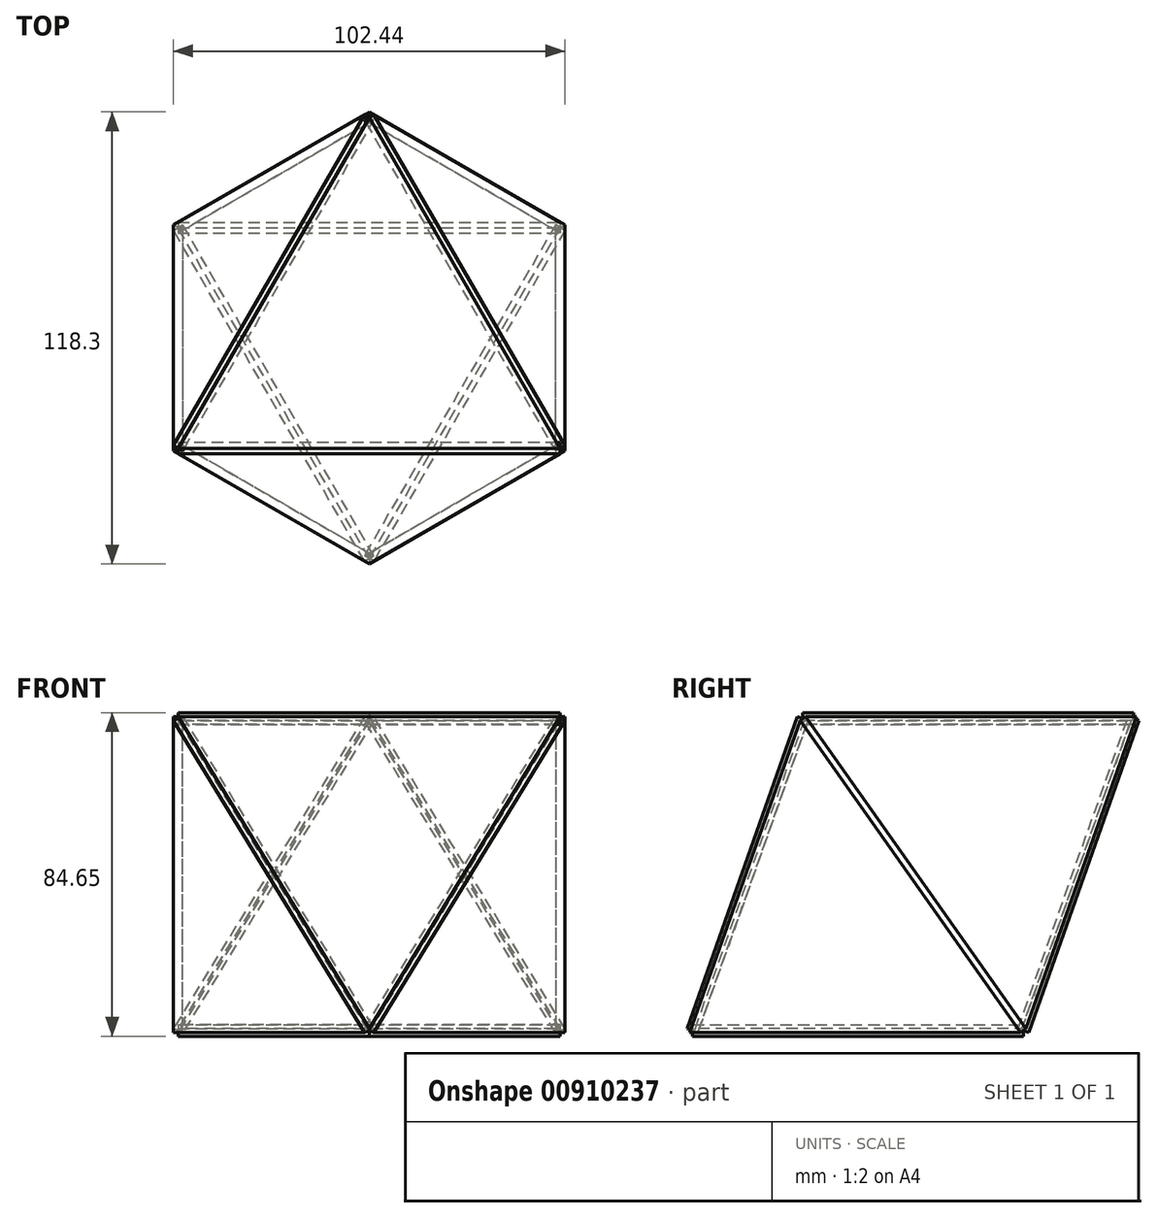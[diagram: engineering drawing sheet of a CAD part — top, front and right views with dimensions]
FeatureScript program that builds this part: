
annotation { "Feature Type Name" : "Feature", "Feature Type Description" : "" }
export const myFeature = defineFeature(function(context is Context, id is Id, definition is map)
    precondition{}
    {
        {
            var Q0;
            Q0=qCreatedBy(makeId("Top.planeOp"),FACE);
            var sketch = newSketch(context, id + "F0", { "sketchPlane" : qUnion([Q0])});
            skCircle(sketch, "E0.cCircle", {"center": v(0, 0) * mm, "radius": 28.87 * mm, "construction": true});
            skLineSegment(sketch, "E0.0", {"start": v(-50, 28.87) * mm, "end": v(50, 28.87) * mm});
            skLineSegment(sketch, "E0.1", {"start": v(50, 28.87) * mm, "end": v(0, -57.74) * mm});
            skLineSegment(sketch, "E0.2", {"start": v(0, -57.74) * mm, "end": v(-50, 28.87) * mm});
            skPoint(sketch, "E0.0.midPoint", {"position": v(0, 28.87) * mm});
            skSolve(sketch);
        }
        {
            var Q0;
            Q0=makeQuery(id+"F0.imprint","IMPRINT",FACE,{"disambiguationData":[TD([[makeQuery(id+"F0.imprint","IMPRINT",EDGE,{"derivedFrom":sQuery(id+"F0.wireOp",EDGE,"E0.0")}),-1.0]])]});
            extrude(context, id + "F1", {"entities" : qUnion([Q0]), "depth" : 3 * mm, "offsetDistance" : 25 * mm});
        }
        {
            var Q0;
            Q0=makeQuery(id+"F1.opExtrude","SWEPT_FACE",FACE,{"disambiguationData":[OSD([sQuery(id+"F0.wireOp",EDGE,"E0.2")])]});
            var sketch = newSketch(context, id + "F2", { "sketchPlane" : qUnion([Q0])});
            skLineSegment(sketch, "E1", {"start": v(-50, 1.5) * mm, "end": v(50, 1.5) * mm});
            skSolve(sketch);
        }
        {
            var Q0;
            Q0=makeQuery(id+"F1.opExtrude","SWEPT_BODY",BODY,{"disambiguationData":[OSD([sQuery(id+"F0.wireOp",EDGE,"E0.0"),sQuery(id+"F0.wireOp",EDGE,"E0.1"),sQuery(id+"F0.wireOp",EDGE,"E0.2")])]});
            transform(context, id + "F3", {"entities" : qUnion([Q0]), "transformType" : TransformType.TRANSLATION_3D, "dx" : 0 * mm, "dy" : 0 * mm, "dz" : 0 * mm, "makeCopy" : true});
        }
        {
            var Q0;
            Q0=makeQuery(id+"F3.opPattern","COPY",BODY,{"derivedFrom":makeQuery(id+"F1.opExtrude","SWEPT_BODY",BODY,{"disambiguationData":[OSD([sQuery(id+"F0.wireOp",EDGE,"E0.0"),sQuery(id+"F0.wireOp",EDGE,"E0.1"),sQuery(id+"F0.wireOp",EDGE,"E0.2")])]}),"instanceName":"1"});
            var Q1;
            Q1=sQuery(id+"F2.wireOp",EDGE,"E1");
            var Q2;
            Q2=sQuery(id+"F2.wireOp",EDGE,"E1");
            transform(context, id + "F4", {"entities" : qUnion([Q0]), "transformType" : TransformType.ROTATION, "transformAxis" : qUnion([Q2]), "angle" : 109.47 * degree, "makeCopy" : false});
        }
        {
            var Q0;
            Q0=makeQuery(id+"F1.opExtrude","SWEPT_BODY",BODY,{"disambiguationData":[OSD([sQuery(id+"F0.wireOp",EDGE,"E0.0"),sQuery(id+"F0.wireOp",EDGE,"E0.1"),sQuery(id+"F0.wireOp",EDGE,"E0.2")])]});
            transform(context, id + "F5", {"entities" : qUnion([Q0]), "transformType" : TransformType.TRANSLATION_3D, "dx" : 0 * mm, "dy" : 0 * mm, "dz" : 0 * mm, "makeCopy" : true});
        }
        {
            var Q0;
            Q0=makeQuery(id+"F1.opExtrude","SWEPT_FACE",FACE,{"disambiguationData":[OSD([sQuery(id+"F0.wireOp",EDGE,"E0.0")])]});
            var sketch = newSketch(context, id + "F6", { "sketchPlane" : qUnion([Q0])});
            skLineSegment(sketch, "E2", {"start": v(50, 1.5) * mm, "end": v(-50, 1.5) * mm});
            skSolve(sketch);
        }
        {
            var Q0;
            Q0=makeQuery(id+"F5.opPattern","COPY",BODY,{"derivedFrom":makeQuery(id+"F1.opExtrude","SWEPT_BODY",BODY,{"disambiguationData":[OSD([sQuery(id+"F0.wireOp",EDGE,"E0.0"),sQuery(id+"F0.wireOp",EDGE,"E0.1"),sQuery(id+"F0.wireOp",EDGE,"E0.2")])]}),"instanceName":"1"});
            var Q1;
            Q1=sQuery(id+"F6.wireOp",EDGE,"E2");
            var Q2;
            Q2=sQuery(id+"F6.wireOp",EDGE,"E2");
            transform(context, id + "F7", {"entities" : qUnion([Q0]), "transformType" : TransformType.ROTATION, "transformAxis" : qUnion([Q2]), "angle" : 109.47 * degree, "oppositeDirection" : true, "makeCopy" : false});
        }
        {
            var Q0;
            Q0=qCreatedBy(makeId("Front.planeOp"),FACE);
            var sketch = newSketch(context, id + "F8", { "sketchPlane" : qUnion([Q0])});
            skLineSegment(sketch, "E3", {"start": v(0, 0) * mm, "end": v(0, 75.98) * mm});
            skSolve(sketch);
        }
        {
            var Q0;
            Q0=makeQuery(id+"F3.opPattern","COPY",BODY,{"derivedFrom":makeQuery(id+"F1.opExtrude","SWEPT_BODY",BODY,{"disambiguationData":[OSD([sQuery(id+"F0.wireOp",EDGE,"E0.0"),sQuery(id+"F0.wireOp",EDGE,"E0.1"),sQuery(id+"F0.wireOp",EDGE,"E0.2")])]}),"instanceName":"1"});
            var Q1;
            Q1=sQuery(id+"F8.wireOp",EDGE,"E3");
            circularPattern(context, id + "F9", {"entities" : qUnion([Q0]), "axis" : qUnion([Q1]), "angle" : 360 * degree, "instanceCount" : 3, "equalSpace" : true});
        }
        {
            var Q0;
            Q0=makeQuery(id+"F5.opPattern","COPY",FACE,{"derivedFrom":makeQuery(id+"F1.opExtrude","SWEPT_FACE",FACE,{"disambiguationData":[OSD([sQuery(id+"F0.wireOp",EDGE,"E0.1")])]}),"instanceName":"1"});
            var sketch = newSketch(context, id + "F10", { "sketchPlane" : qUnion([Q0])});
            skLineSegment(sketch, "E4", {"start": v(21.03, -22.59) * mm, "end": v(50.3, 73.03) * mm});
            skSolve(sketch);
        }
        {
            var Q0;
            Q0=makeQuery(id+"F5.opPattern","COPY",BODY,{"derivedFrom":makeQuery(id+"F1.opExtrude","SWEPT_BODY",BODY,{"disambiguationData":[OSD([sQuery(id+"F0.wireOp",EDGE,"E0.0"),sQuery(id+"F0.wireOp",EDGE,"E0.1"),sQuery(id+"F0.wireOp",EDGE,"E0.2")])]}),"instanceName":"1"});
            var Q1;
            Q1=sQuery(id+"F10.wireOp",EDGE,"E4");
            transform(context, id + "F11", {"entities" : qUnion([Q0]), "transformType" : TransformType.ROTATION, "transformAxis" : qUnion([Q1]), "angle" : 109.47 * degree, "makeCopy" : false});
        }
        {
            var Q0;
            Q0=makeQuery(id+"F5.opPattern","COPY",BODY,{"derivedFrom":makeQuery(id+"F1.opExtrude","SWEPT_BODY",BODY,{"disambiguationData":[OSD([sQuery(id+"F0.wireOp",EDGE,"E0.0"),sQuery(id+"F0.wireOp",EDGE,"E0.1"),sQuery(id+"F0.wireOp",EDGE,"E0.2")])]}),"instanceName":"1"});
            var Q1;
            Q1=sQuery(id+"F8.wireOp",EDGE,"E3");
            circularPattern(context, id + "F12", {"entities" : qUnion([Q0]), "axis" : qUnion([Q1]), "angle" : 360 * degree, "instanceCount" : 3, "equalSpace" : true});
        }
        {
            var Q0;
            Q0=makeQuery(id+"F5.opPattern","COPY",FACE,{"derivedFrom":makeQuery(id+"F1.opExtrude","SWEPT_FACE",FACE,{"disambiguationData":[OSD([sQuery(id+"F0.wireOp",EDGE,"E0.2")])]}),"instanceName":"1"});
            var sketch = newSketch(context, id + "F13", { "sketchPlane" : qUnion([Q0])});
            skLineSegment(sketch, "E5", {"start": v(20.74, 71.33) * mm, "end": v(72.96, -13.95) * mm});
            skSolve(sketch);
        }
        {
            var Q0;
            Q0=makeQuery(id+"F5.opPattern","COPY",BODY,{"derivedFrom":makeQuery(id+"F1.opExtrude","SWEPT_BODY",BODY,{"disambiguationData":[OSD([sQuery(id+"F0.wireOp",EDGE,"E0.0"),sQuery(id+"F0.wireOp",EDGE,"E0.1"),sQuery(id+"F0.wireOp",EDGE,"E0.2")])]}),"instanceName":"1"});
            transform(context, id + "F14", {"entities" : qUnion([Q0]), "transformType" : TransformType.TRANSLATION_3D, "dx" : 0 * mm, "dy" : 0 * mm, "dz" : 0 * mm, "makeCopy" : true});
        }
        {
            var Q0;
            Q0=makeQuery(id+"F14.opPattern","COPY",BODY,{"derivedFrom":makeQuery(id+"F5.opPattern","COPY",BODY,{"derivedFrom":makeQuery(id+"F1.opExtrude","SWEPT_BODY",BODY,{"disambiguationData":[OSD([sQuery(id+"F0.wireOp",EDGE,"E0.0"),sQuery(id+"F0.wireOp",EDGE,"E0.1"),sQuery(id+"F0.wireOp",EDGE,"E0.2")])]}),"instanceName":"1"}),"instanceName":"1"});
            var Q1;
            Q1=sQuery(id+"F13.wireOp",EDGE,"E5");
            var Q2;
            Q2=sQuery(id+"F13.wireOp",EDGE,"E5");
            transform(context, id + "F15", {"entities" : qUnion([Q0]), "transformType" : TransformType.ROTATION, "transformAxis" : qUnion([Q2]), "angle" : 109.47 * degree, "oppositeDirection" : true, "makeCopy" : false});
        }
    });
